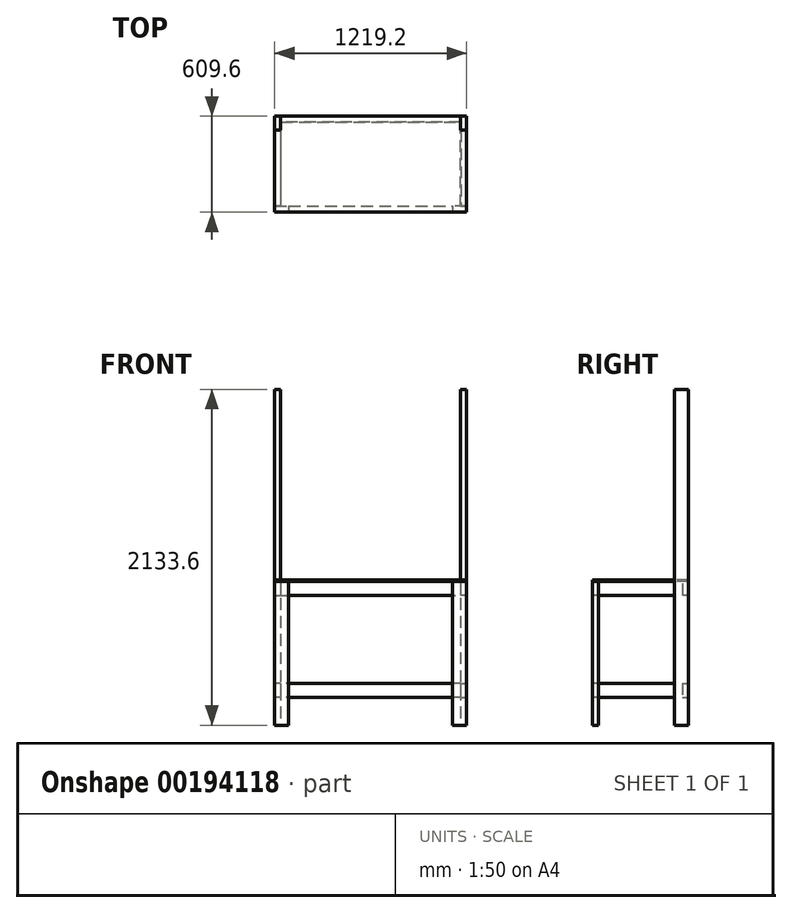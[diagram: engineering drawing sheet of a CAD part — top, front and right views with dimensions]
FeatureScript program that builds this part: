
annotation { "Feature Type Name" : "Feature", "Feature Type Description" : "" }
export const myFeature = defineFeature(function(context is Context, id is Id, definition is map)
    precondition{}
    {
        {
            var Q0;
            Q0=qCreatedBy(makeId("Top.planeOp"),FACE);
            var sketch = newSketch(context, id + "F0", { "sketchPlane" : qUnion([Q0])});
            skLineSegment(sketch, "E0.bottom", {"start": v(-609.6, 304.8) * mm, "end": v(609.6, 304.8) * mm, "construction": true});
            skLineSegment(sketch, "E0.top", {"start": v(-609.6, -304.8) * mm, "end": v(609.6, -304.8) * mm, "construction": true});
            skLineSegment(sketch, "E0.left", {"start": v(-609.6, 304.8) * mm, "end": v(-609.6, -304.8) * mm, "construction": true});
            skLineSegment(sketch, "E0.right", {"start": v(609.6, 304.8) * mm, "end": v(609.6, -304.8) * mm, "construction": true});
            skLineSegment(sketch, "E1.bottom", {"start": v(-609.6, 304.8) * mm, "end": v(-571.5, 304.8) * mm});
            skLineSegment(sketch, "E1.top", {"start": v(-609.6, 215.9) * mm, "end": v(-571.5, 215.9) * mm});
            skLineSegment(sketch, "E1.left", {"start": v(-609.6, 304.8) * mm, "end": v(-609.6, 215.9) * mm});
            skLineSegment(sketch, "E1.right", {"start": v(-571.5, 304.8) * mm, "end": v(-571.5, 215.9) * mm});
            skLineSegment(sketch, "E2.bottom", {"start": v(609.6, 304.8) * mm, "end": v(571.5, 304.8) * mm});
            skLineSegment(sketch, "E2.top", {"start": v(609.6, 215.9) * mm, "end": v(571.5, 215.9) * mm});
            skLineSegment(sketch, "E2.left", {"start": v(609.6, 304.8) * mm, "end": v(609.6, 215.9) * mm});
            skLineSegment(sketch, "E2.right", {"start": v(571.5, 304.8) * mm, "end": v(571.5, 215.9) * mm});
            skLineSegment(sketch, "E3.bottom", {"start": v(609.6, -304.8) * mm, "end": v(520.7, -304.8) * mm});
            skLineSegment(sketch, "E3.top", {"start": v(609.6, -266.7) * mm, "end": v(520.7, -266.7) * mm});
            skLineSegment(sketch, "E3.left", {"start": v(609.6, -304.8) * mm, "end": v(609.6, -266.7) * mm});
            skLineSegment(sketch, "E3.right", {"start": v(520.7, -304.8) * mm, "end": v(520.7, -266.7) * mm});
            skLineSegment(sketch, "E4.bottom", {"start": v(-609.6, -304.8) * mm, "end": v(-520.7, -304.8) * mm});
            skLineSegment(sketch, "E4.top", {"start": v(-609.6, -266.7) * mm, "end": v(-520.7, -266.7) * mm});
            skLineSegment(sketch, "E4.left", {"start": v(-609.6, -304.8) * mm, "end": v(-609.6, -266.7) * mm});
            skLineSegment(sketch, "E4.right", {"start": v(-520.7, -304.8) * mm, "end": v(-520.7, -266.7) * mm});
            skSolve(sketch);
        }
        {
            var Q0;
            Q0=makeQuery(id+"F0.imprint","IMPRINT",FACE,{"disambiguationData":[TD([[makeQuery(id+"F0.imprint","IMPRINT",EDGE,{"derivedFrom":sQuery(id+"F0.wireOp",EDGE,"E1.bottom")}),-1.0]])]});
            var Q1;
            Q1=makeQuery(id+"F0.imprint","IMPRINT",FACE,{"disambiguationData":[TD([[makeQuery(id+"F0.imprint","IMPRINT",EDGE,{"derivedFrom":sQuery(id+"F0.wireOp",EDGE,"E2.bottom")}),1.0]])]});
            extrude(context, id + "F1", {"entities" : qUnion([Q0, Q1]), "depth" : 2133.6 * mm});
        }
        {
            var Q0;
            Q0=makeQuery(id+"F0.imprint","IMPRINT",FACE,{"disambiguationData":[TD([[makeQuery(id+"F0.imprint","IMPRINT",EDGE,{"derivedFrom":sQuery(id+"F0.wireOp",EDGE,"E4.bottom")}),1.0]])]});
            var Q1;
            Q1=makeQuery(id+"F0.imprint","IMPRINT",FACE,{"disambiguationData":[TD([[makeQuery(id+"F0.imprint","IMPRINT",EDGE,{"derivedFrom":sQuery(id+"F0.wireOp",EDGE,"E3.bottom")}),-1.0]])]});
            extrude(context, id + "F2", {"entities" : qUnion([Q0, Q1]), "depth" : 914.4 * mm});
        }
        {
            var Q0;
            Q0=makeQuery(id+"F2.opExtrude","SWEPT_FACE",FACE,{"disambiguationData":[OSD([sQuery(id+"F0.wireOp",EDGE,"E4.bottom")])]});
            var sketch = newSketch(context, id + "F3", { "sketchPlane" : qUnion([Q0])});
            skLineSegment(sketch, "E5.bottom", {"start": v(-609.6, 0) * mm, "end": v(602.1, 0) * mm, "construction": true});
            skLineSegment(sketch, "E5.top", {"start": v(-609.6, 177.8) * mm, "end": v(602.1, 177.8) * mm, "construction": true});
            skLineSegment(sketch, "E5.left", {"start": v(-609.6, 0) * mm, "end": v(-609.6, 177.8) * mm, "construction": true});
            skLineSegment(sketch, "E5.right", {"start": v(602.1, 0) * mm, "end": v(602.1, 177.8) * mm, "construction": true});
            skLineSegment(sketch, "E6.bottom", {"start": v(-520.7, 177.8) * mm, "end": v(520.7, 177.8) * mm});
            skLineSegment(sketch, "E6.top", {"start": v(-520.7, 266.7) * mm, "end": v(520.7, 266.7) * mm});
            skLineSegment(sketch, "E6.left", {"start": v(-520.7, 177.8) * mm, "end": v(-520.7, 266.7) * mm});
            skLineSegment(sketch, "E6.right", {"start": v(520.7, 177.8) * mm, "end": v(520.7, 266.7) * mm});
            skSolve(sketch);
        }
        {
            var Q0;
            Q0=makeQuery(id+"F3.imprint","IMPRINT",FACE,{"disambiguationData":[TD([[makeQuery(id+"F3.imprint","IMPRINT",EDGE,{"derivedFrom":sQuery(id+"F3.wireOp",EDGE,"E6.bottom")}),1.0]])]});
            extrude(context, id + "F4", {"entities" : qUnion([Q0]), "oppositeDirection" : true, "depth" : 38.1 * mm});
        }
        {
            var Q0;
            Q0=makeQuery(id+"F2.opExtrude","SWEPT_FACE",FACE,{"disambiguationData":[OSD([sQuery(id+"F0.wireOp",EDGE,"E3.left")])]});
            var sketch = newSketch(context, id + "F5", { "sketchPlane" : qUnion([Q0])});
            skLineSegment(sketch, "E7.bottom", {"start": v(-304.8, 0) * mm, "end": v(553.73, 0) * mm, "construction": true});
            skLineSegment(sketch, "E7.top", {"start": v(-304.8, 177.8) * mm, "end": v(553.73, 177.8) * mm, "construction": true});
            skLineSegment(sketch, "E7.left", {"start": v(-304.8, 0) * mm, "end": v(-304.8, 177.8) * mm, "construction": true});
            skLineSegment(sketch, "E7.right", {"start": v(553.73, 0) * mm, "end": v(553.73, 177.8) * mm, "construction": true});
            skLineSegment(sketch, "E8.bottom", {"start": v(-266.7, 177.8) * mm, "end": v(215.9, 177.8) * mm});
            skLineSegment(sketch, "E8.top", {"start": v(-266.7, 266.7) * mm, "end": v(215.9, 266.7) * mm});
            skLineSegment(sketch, "E8.left", {"start": v(-266.7, 177.8) * mm, "end": v(-266.7, 266.7) * mm});
            skLineSegment(sketch, "E8.right", {"start": v(215.9, 177.8) * mm, "end": v(215.9, 266.7) * mm});
            skSolve(sketch);
        }
        {
            var Q0;
            Q0=makeQuery(id+"F5.imprint","IMPRINT",FACE,{"disambiguationData":[TD([[makeQuery(id+"F5.imprint","IMPRINT",EDGE,{"derivedFrom":sQuery(id+"F5.wireOp",EDGE,"E8.bottom")}),1.0]])]});
            extrude(context, id + "F6", {"entities" : qUnion([Q0]), "oppositeDirection" : true, "depth" : 38.1 * mm});
        }
        {
            var Q0;
            Q0=makeQuery(id+"F1.opExtrude","SWEPT_FACE",FACE,{"disambiguationData":[OSD([sQuery(id+"F0.wireOp",EDGE,"E2.bottom")])]});
            var sketch = newSketch(context, id + "F7", { "sketchPlane" : qUnion([Q0])});
            skLineSegment(sketch, "E9.bottom", {"start": v(-609.6, 0) * mm, "end": v(676.26, 0) * mm, "construction": true});
            skLineSegment(sketch, "E9.top", {"start": v(-609.6, 177.8) * mm, "end": v(676.26, 177.8) * mm, "construction": true});
            skLineSegment(sketch, "E9.left", {"start": v(-609.6, 0) * mm, "end": v(-609.6, 177.8) * mm, "construction": true});
            skLineSegment(sketch, "E9.right", {"start": v(676.26, 0) * mm, "end": v(676.26, 177.8) * mm, "construction": true});
            skLineSegment(sketch, "E10.bottom", {"start": v(-571.5, 177.8) * mm, "end": v(571.5, 177.8) * mm});
            skLineSegment(sketch, "E10.top", {"start": v(-571.5, 266.7) * mm, "end": v(571.5, 266.7) * mm});
            skLineSegment(sketch, "E10.left", {"start": v(-571.5, 177.8) * mm, "end": v(-571.5, 266.7) * mm});
            skLineSegment(sketch, "E10.right", {"start": v(571.5, 177.8) * mm, "end": v(571.5, 266.7) * mm});
            skSolve(sketch);
        }
        {
            var Q0;
            Q0 = qSketchRegion(id + "F7", true);
            extrude(context, id + "F8", {"entities" : qUnion([Q0]), "oppositeDirection" : true, "depth" : 38.1 * mm});
        }
        {
            var Q0;
            Q0=makeQuery(id+"F1.opExtrude","SWEPT_FACE",FACE,{"disambiguationData":[OSD([sQuery(id+"F0.wireOp",EDGE,"E1.left")])]});
            var sketch = newSketch(context, id + "F9", { "sketchPlane" : qUnion([Q0])});
            skLineSegment(sketch, "E11.bottom", {"start": v(-304.8, 0) * mm, "end": v(286.26, 0) * mm, "construction": true});
            skLineSegment(sketch, "E11.top", {"start": v(-304.8, 177.8) * mm, "end": v(286.26, 177.8) * mm, "construction": true});
            skLineSegment(sketch, "E11.left", {"start": v(-304.8, 0) * mm, "end": v(-304.8, 177.8) * mm, "construction": true});
            skLineSegment(sketch, "E11.right", {"start": v(286.26, 0) * mm, "end": v(286.26, 177.8) * mm, "construction": true});
            skLineSegment(sketch, "E12.bottom", {"start": v(-215.9, 177.8) * mm, "end": v(266.7, 177.8) * mm});
            skLineSegment(sketch, "E12.top", {"start": v(-215.9, 266.7) * mm, "end": v(266.7, 266.7) * mm});
            skLineSegment(sketch, "E12.left", {"start": v(-215.9, 177.8) * mm, "end": v(-215.9, 266.7) * mm});
            skLineSegment(sketch, "E12.right", {"start": v(266.7, 177.8) * mm, "end": v(266.7, 266.7) * mm});
            skSolve(sketch);
        }
        {
            var Q0;
            Q0=makeQuery(id+"F9.imprint","IMPRINT",FACE,{"disambiguationData":[TD([[makeQuery(id+"F9.imprint","IMPRINT",EDGE,{"derivedFrom":sQuery(id+"F9.wireOp",EDGE,"E12.bottom")}),1.0]])]});
            extrude(context, id + "F10", {"entities" : qUnion([Q0]), "oppositeDirection" : true, "depth" : 38.1 * mm});
        }
        {
            var Q0;
            Q0=makeQuery(id+"F2.opExtrude","CAP_FACE",FACE,{"disambiguationData":[OSD([sQuery(id+"F0.wireOp",EDGE,"E4.bottom"),sQuery(id+"F0.wireOp",EDGE,"E4.top"),sQuery(id+"F0.wireOp",EDGE,"E4.left"),sQuery(id+"F0.wireOp",EDGE,"E4.right")])],"isStart":false});
            var sketch = newSketch(context, id + "F11", { "sketchPlane" : qUnion([Q0])});
            skLineSegment(sketch, "E13.bottom", {"start": v(-609.6, -304.8) * mm, "end": v(609.6, -304.8) * mm, "construction": true});
            skLineSegment(sketch, "E13.top", {"start": v(-609.6, 304.8) * mm, "end": v(609.6, 304.8) * mm, "construction": true});
            skLineSegment(sketch, "E13.left", {"start": v(-609.6, -304.8) * mm, "end": v(-609.6, 304.8) * mm, "construction": true});
            skLineSegment(sketch, "E13.right", {"start": v(609.6, -304.8) * mm, "end": v(609.6, 304.8) * mm, "construction": true});
            skLineSegment(sketch, "E14.bottom", {"start": v(-609.6, -266.7) * mm, "end": v(-570.84, -266.7) * mm});
            skLineSegment(sketch, "E14.top", {"start": v(-609.6, 215.9) * mm, "end": v(-570.84, 215.9) * mm});
            skLineSegment(sketch, "E14.left", {"start": v(-609.6, -266.7) * mm, "end": v(-609.6, 215.9) * mm});
            skLineSegment(sketch, "E14.right", {"start": v(-570.84, -266.7) * mm, "end": v(-570.84, 215.9) * mm});
            skLineSegment(sketch, "E15.bottom", {"start": v(-570.84, 304.8) * mm, "end": v(572.16, 304.8) * mm});
            skLineSegment(sketch, "E15.top", {"start": v(-570.84, 267.05) * mm, "end": v(572.16, 267.05) * mm});
            skLineSegment(sketch, "E15.left", {"start": v(-570.84, 304.8) * mm, "end": v(-570.84, 267.05) * mm});
            skLineSegment(sketch, "E15.right", {"start": v(572.16, 304.8) * mm, "end": v(572.16, 267.05) * mm});
            skLineSegment(sketch, "E16.bottom", {"start": v(609.6, 215.9) * mm, "end": v(572.16, 215.9) * mm});
            skLineSegment(sketch, "E16.top", {"start": v(609.6, -266.7) * mm, "end": v(572.16, -266.7) * mm});
            skLineSegment(sketch, "E16.left", {"start": v(609.6, 215.9) * mm, "end": v(609.6, -266.7) * mm});
            skLineSegment(sketch, "E16.right", {"start": v(572.16, 215.9) * mm, "end": v(572.16, -266.7) * mm});
            skLineSegment(sketch, "E17.bottom", {"start": v(520.7, -266.7) * mm, "end": v(-520.7, -266.7) * mm});
            skLineSegment(sketch, "E17.top", {"start": v(520.7, -304.8) * mm, "end": v(-520.7, -304.8) * mm});
            skLineSegment(sketch, "E17.left", {"start": v(520.7, -266.7) * mm, "end": v(520.7, -304.8) * mm});
            skLineSegment(sketch, "E17.right", {"start": v(-520.7, -266.7) * mm, "end": v(-520.7, -304.8) * mm});
            skSolve(sketch);
        }
        {
            var Q0;
            Q0 = qSketchRegion(id + "F11", true);
            extrude(context, id + "F12", {"entities" : qUnion([Q0]), "oppositeDirection" : true, "depth" : 88.9 * mm});
        }
        {
            var Q0;
            Q0=makeQuery(id+"F2.opExtrude","CAP_FACE",FACE,{"disambiguationData":[OSD([sQuery(id+"F0.wireOp",EDGE,"E4.bottom"),sQuery(id+"F0.wireOp",EDGE,"E4.top"),sQuery(id+"F0.wireOp",EDGE,"E4.left"),sQuery(id+"F0.wireOp",EDGE,"E4.right")])],"isStart":false});
            var sketch = newSketch(context, id + "F13", { "sketchPlane" : qUnion([Q0])});
            skLineSegment(sketch, "E18", {"start": v(-609.6, -304.8) * mm, "end": v(-609.6, 215.9) * mm, "construction": true});
            skLineSegment(sketch, "E19", {"start": v(-609.6, 215.9) * mm, "end": v(-571.5, 215.9) * mm});
            skLineSegment(sketch, "E20", {"start": v(-571.5, 215.9) * mm, "end": v(-571.5, 304.8) * mm});
            skLineSegment(sketch, "E21", {"start": v(-571.5, 304.8) * mm, "end": v(571.5, 304.8) * mm});
            skLineSegment(sketch, "E22", {"start": v(571.5, 304.8) * mm, "end": v(571.5, 215.9) * mm});
            skLineSegment(sketch, "E23", {"start": v(571.5, 215.9) * mm, "end": v(609.6, 215.9) * mm});
            skLineSegment(sketch, "E24", {"start": v(609.6, 215.9) * mm, "end": v(609.6, -304.8) * mm});
            skLineSegment(sketch, "E25", {"start": v(609.6, -304.8) * mm, "end": v(-609.6, -304.8) * mm});
            skLineSegment(sketch, "E26", {"start": v(-609.6, 215.9) * mm, "end": v(-609.6, -304.8) * mm});
            skSolve(sketch);
        }
        {
            var Q0;
            Q0 = qSketchRegion(id + "F13", true);
            extrude(context, id + "F14", {"entities" : qUnion([Q0]), "depth" : 9.52 * mm});
        }
    });
